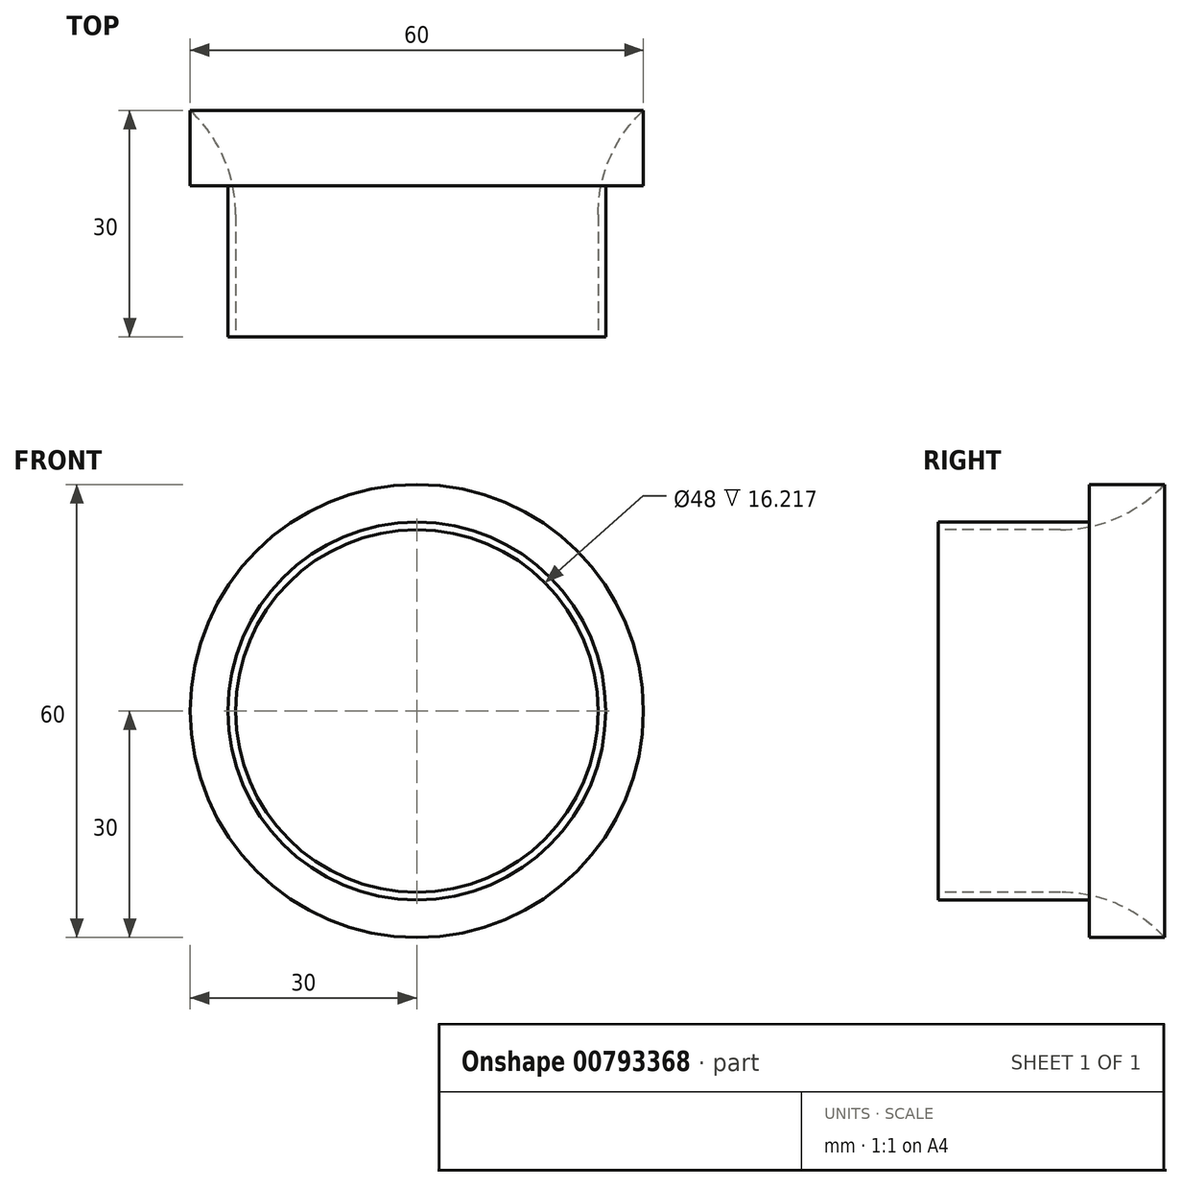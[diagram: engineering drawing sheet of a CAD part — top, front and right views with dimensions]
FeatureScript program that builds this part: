
annotation { "Feature Type Name" : "Feature", "Feature Type Description" : "" }
export const myFeature = defineFeature(function(context is Context, id is Id, definition is map)
    precondition{}
    {
        {
            var Q0;
            Q0=qCreatedBy(makeId("Front.planeOp"),FACE);
            var sketch = newSketch(context, id + "F0", { "sketchPlane" : qUnion([Q0])});
            skCircle(sketch, "E0", {"center": v(0, 0) * mm, "radius": 30 * mm});
            skSolve(sketch);
        }
        {
            var Q0;
            Q0 = qSketchRegion(id + "F0", true);
            extrude(context, id + "F1", {"entities" : qUnion([Q0]), "oppositeDirection" : true, "depth" : 50 * mm, "offsetDistance" : 25 * mm});
        }
        {
            var Q0;
            Q0=makeQuery(id+"F1.opExtrude","CAP_FACE",FACE,{"disambiguationData":[OSD([sQuery(id+"F0.wireOp",EDGE,"E0")])],"isStart":true});
            var sketch = newSketch(context, id + "F2", { "sketchPlane" : qUnion([Q0])});
            skCircle(sketch, "E1", {"center": v(0, 0) * mm, "radius": 25 * mm});
            skSolve(sketch);
        }
        {
            var Q0;
            Q0=makeQuery(id+"F2.imprint","IMPRINT",FACE,{"disambiguationData":[TD([[makeQuery(id+"F2.imprint","IMPRINT",EDGE,{"derivedFrom":sQuery(id+"F2.wireOp",EDGE,"E1")}),-1.0]])]});
            extrude(context, id + "F3", {"entities" : qUnion([Q0]), "operationType" : NewBodyOperationType.REMOVE, "oppositeDirection" : true, "depth" : 40 * mm, "offsetDistance" : 25 * mm});
        }
        {
            var Q0;
            Q0=makeQuery(id+"F1.opExtrude","CAP_FACE",FACE,{"disambiguationData":[OSD([sQuery(id+"F0.wireOp",EDGE,"E0")])],"isStart":true});
            var sketch = newSketch(context, id + "F4", { "sketchPlane" : qUnion([Q0])});
            skCircle(sketch, "E2", {"center": v(0, 0) * mm, "radius": 24 * mm});
            skSolve(sketch);
        }
        {
            var Q0;
            Q0 = qSketchRegion(id + "F4", true);
            extrude(context, id + "F5", {"entities" : qUnion([Q0]), "operationType" : NewBodyOperationType.REMOVE, "oppositeDirection" : true, "depth" : 60 * mm, "offsetDistance" : 25 * mm});
        }
        {
            var Q0;
            Q0=makeQuery(id+"F5.boolean.opBoolean","INTERSECT",EDGE,{"derivedFrom":[makeQuery(id+"F1.opExtrude","CAP_FACE",FACE,{"disambiguationData":[OSD([sQuery(id+"F0.wireOp",EDGE,"E0")])],"isStart":false}),makeQuery(id+"F5.opExtrude","SWEPT_FACE",FACE,{"disambiguationData":[OSD([sQuery(id+"F4.wireOp",EDGE,"E2")])]})]});
            fillet(context, id + "F6", {"entities" : qUnion([Q0]), "radius" : 18.83 * mm, "tangentPropagation" : true, "defaultsChanged" : false, "vertexSettings" : [], "allowEdgeOverflow" : false});
        }
        {
            var Q0;
            Q0=makeQuery(id+"F1.opExtrude","CAP_FACE",FACE,{"disambiguationData":[OSD([sQuery(id+"F0.wireOp",EDGE,"E0")])],"isStart":true});
            extrude(context, id + "F7", {"entities" : qUnion([Q0]), "operationType" : NewBodyOperationType.REMOVE, "oppositeDirection" : true, "depth" : 20 * mm, "offsetDistance" : 25 * mm});
        }
    });
